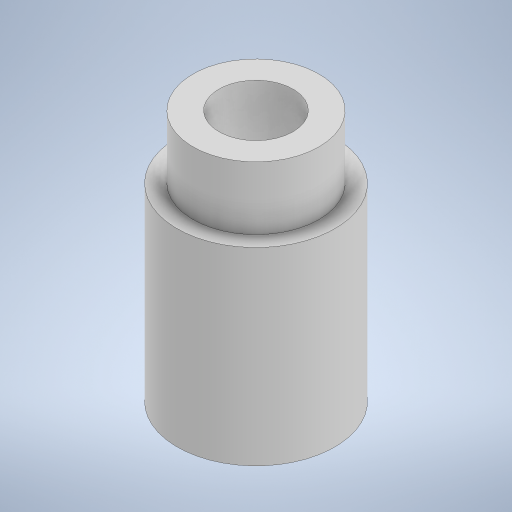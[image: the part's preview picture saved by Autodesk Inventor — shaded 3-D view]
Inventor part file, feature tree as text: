
AUTODESK INVENTOR PART (.ipt)
format: ipt  version: 2024.2 (Build 282272000, 272)  size: 229,888 bytes
history: native  units: mm
features: extrude x2, sketch x2
ambient origin geometry x8: Origin, YZ Plane, XZ Plane, XY Plane, X Axis, Y Axis, Z Axis, Center Point
bodies: Solid1 (feature_tree)
feature tree (4):
  extrude  "Extrusion1"  Depth=10.0mm
  extrude  "Extrusion2"  Depth=4.0mm
  sketch  "Sketch1"  dims[d0=4.7mm d1=10.0mm]
  sketch  "Sketch2"  dims[d2=12.0mm d3=0.0mm d4=8.0mm d5=4.0mm d6=0.0mm]
